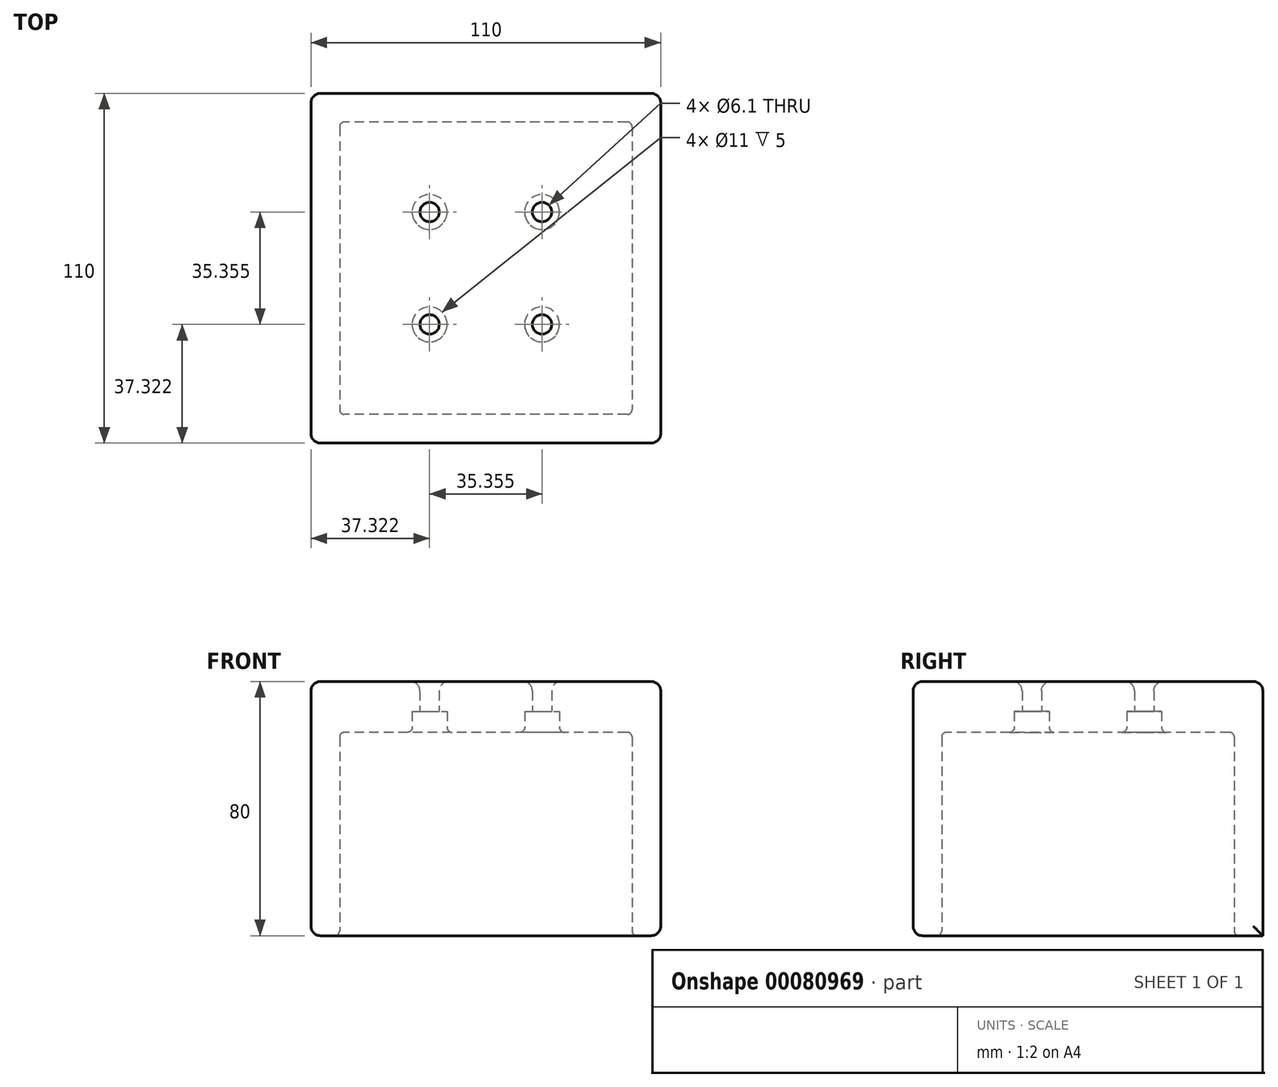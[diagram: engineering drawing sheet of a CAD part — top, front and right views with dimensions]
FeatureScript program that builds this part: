
annotation { "Feature Type Name" : "Feature", "Feature Type Description" : "" }
export const myFeature = defineFeature(function(context is Context, id is Id, definition is map)
    precondition{}
    {
        {
            var Q0;
            Q0=qCreatedBy(makeId("Top.planeOp"),FACE);
            var sketch = newSketch(context, id + "F0", { "sketchPlane" : qUnion([Q0])});
            skLineSegment(sketch, "E0.bottom", {"start": v(55, 55) * mm, "end": v(-55, 55) * mm});
            skLineSegment(sketch, "E0.top", {"start": v(55, -55) * mm, "end": v(-55, -55) * mm});
            skLineSegment(sketch, "E0.left", {"start": v(55, 55) * mm, "end": v(55, -55) * mm});
            skLineSegment(sketch, "E0.right", {"start": v(-55, 55) * mm, "end": v(-55, -55) * mm});
            skPoint(sketch, "E0.middle", {"position": v(0, 0) * mm});
            skLineSegment(sketch, "E1.bottom", {"start": v(46, 46) * mm, "end": v(-46, 46) * mm});
            skLineSegment(sketch, "E1.top", {"start": v(46, -46) * mm, "end": v(-46, -46) * mm});
            skLineSegment(sketch, "E1.left", {"start": v(46, 46) * mm, "end": v(46, -46) * mm});
            skLineSegment(sketch, "E1.right", {"start": v(-46, 46) * mm, "end": v(-46, -46) * mm});
            skSolve(sketch);
        }
        {
            var Q0;
            Q0=makeQuery(id+"F0.imprint","IMPRINT",FACE,{"disambiguationData":[TD([[makeQuery(id+"F0.imprint","IMPRINT",EDGE,{"derivedFrom":sQuery(id+"F0.wireOp",EDGE,"E0.bottom")}),1.0]])]});
            var Q1;
            Q1=makeQuery(id+"F0.imprint","IMPRINT",FACE,{"disambiguationData":[TD([[makeQuery(id+"F0.imprint","IMPRINT",EDGE,{"derivedFrom":sQuery(id+"F0.wireOp",EDGE,"E1.bottom")}),1.0]])]});
            extrude(context, id + "F1", {"entities" : qUnion([Q0, Q1]), "depth" : 80 * mm});
        }
        {
            var Q0;
            Q0=makeQuery(id+"F0.imprint","IMPRINT",FACE,{"disambiguationData":[TD([[makeQuery(id+"F0.imprint","IMPRINT",EDGE,{"derivedFrom":sQuery(id+"F0.wireOp",EDGE,"E1.bottom")}),1.0]])]});
            extrude(context, id + "F2", {"entities" : qUnion([Q0]), "operationType" : NewBodyOperationType.REMOVE, "depth" : 64 * mm});
        }
        {
            var Q0;
            Q0=makeQuery(id+"F2.boolean.opBoolean","COPY",FACE,{"derivedFrom":makeQuery(id+"F2.opExtrude","CAP_FACE",FACE,{"disambiguationData":[OSD([sQuery(id+"F0.wireOp",EDGE,"E1.bottom"),sQuery(id+"F0.wireOp",EDGE,"E1.top"),sQuery(id+"F0.wireOp",EDGE,"E1.left"),sQuery(id+"F0.wireOp",EDGE,"E1.right")])],"isStart":false})});
            var sketch = newSketch(context, id + "F3", { "sketchPlane" : qUnion([Q0])});
            skLineSegment(sketch, "E2", {"start": v(0, 0) * mm, "end": v(46, -46) * mm});
            skPoint(sketch, "E3", {"position": v(17.68, -17.68) * mm});
            skPoint(sketch, "E4.1.0", {"position": v(17.68, 17.68) * mm});
            skPoint(sketch, "E4.2.0", {"position": v(-17.68, 17.68) * mm});
            skPoint(sketch, "E4.3.0", {"position": v(-17.68, -17.68) * mm});
            skPoint(sketch, "E4.center", {"position": v(0, 0) * mm});
            skSolve(sketch);
        }
        {
            var Q0;
            Q0=sQuery(id+"F3.wireOp",VERTEX,"E4.1.0");
            var Q1;
            Q1=sQuery(id+"F3.wireOp",VERTEX,"E3");
            var Q2;
            Q2=sQuery(id+"F3.wireOp",VERTEX,"E4.3.0");
            var Q3;
            Q3=sQuery(id+"F3.wireOp",VERTEX,"E4.2.0");
            var Q4;
            Q4=makeQuery(id+"F1.opExtrude","SWEPT_BODY",BODY,{"disambiguationData":[OSD([sQuery(id+"F0.wireOp",EDGE,"E0.bottom"),sQuery(id+"F0.wireOp",EDGE,"E0.top"),sQuery(id+"F0.wireOp",EDGE,"E0.left"),sQuery(id+"F0.wireOp",EDGE,"E0.right")])]});
            hole(context, id + "F4", {"style" : HoleStyle.C_BORE, "endStyle" : HoleEndStyle.THROUGH, "holeDiameter" : 6.1 * mm, "cBoreDiameter" : 11 * mm, "cBoreDepth" : 6.5 * mm, "locations" : qUnion([Q0, Q1, Q2, Q3]), "scope" : qUnion([Q4]), "isTappedThrough" : true});
        }
        {
            var Q0;
            Q0=makeQuery(id+"F1.opExtrude","CAP_FACE",FACE,{"disambiguationData":[OSD([sQuery(id+"F0.wireOp",EDGE,"E0.bottom"),sQuery(id+"F0.wireOp",EDGE,"E0.top"),sQuery(id+"F0.wireOp",EDGE,"E0.left"),sQuery(id+"F0.wireOp",EDGE,"E0.right")])],"isStart":false});
            var Q1;
            Q1=makeQuery(id+"F1.opExtrude","SWEPT_FACE",FACE,{"disambiguationData":[OSD([sQuery(id+"F0.wireOp",EDGE,"E0.left")])]});
            var Q2;
            Q2=makeQuery(id+"F1.opExtrude","CAP_EDGE",EDGE,{"disambiguationData":[OSD([sQuery(id+"F0.wireOp",EDGE,"E0.right")])],"isStart":true});
            var Q3;
            Q3=makeQuery(id+"F1.opExtrude","SWEPT_FACE",FACE,{"disambiguationData":[OSD([sQuery(id+"F0.wireOp",EDGE,"E0.right")])]});
            var Q4;
            Q4=makeQuery(id+"F1.opExtrude","SWEPT_FACE",FACE,{"disambiguationData":[OSD([sQuery(id+"F0.wireOp",EDGE,"E0.top")])]});
            fillet(context, id + "F5", {"entities" : qUnion([Q0, Q1, Q2, Q3, Q4]), "radius" : 3 * mm, "tangentPropagation" : true, "allowEdgeOverflow" : false});
        }
        {
            var Q0;
            Q0=makeQuery(id+"F2.boolean.opBoolean","COPY",FACE,{"derivedFrom":makeQuery(id+"F2.opExtrude","CAP_FACE",FACE,{"disambiguationData":[OSD([sQuery(id+"F0.wireOp",EDGE,"E1.bottom"),sQuery(id+"F0.wireOp",EDGE,"E1.top"),sQuery(id+"F0.wireOp",EDGE,"E1.left"),sQuery(id+"F0.wireOp",EDGE,"E1.right")])],"isStart":false})});
            var Q1;
            Q1=makeQuery(id+"F2.boolean.opBoolean","COPY",FACE,{"derivedFrom":makeQuery(id+"F2.opExtrude","SWEPT_FACE",FACE,{"disambiguationData":[OSD([sQuery(id+"F0.wireOp",EDGE,"E1.top")])]})});
            var Q2;
            Q2=makeQuery(id+"F2.boolean.opBoolean","COPY",FACE,{"derivedFrom":makeQuery(id+"F2.opExtrude","SWEPT_FACE",FACE,{"disambiguationData":[OSD([sQuery(id+"F0.wireOp",EDGE,"E1.left")])]})});
            var Q3;
            Q3=makeQuery(id+"F2.boolean.opBoolean","COPY",FACE,{"derivedFrom":makeQuery(id+"F2.opExtrude","SWEPT_FACE",FACE,{"disambiguationData":[OSD([sQuery(id+"F0.wireOp",EDGE,"E1.right")])]})});
            var Q4;
            Q4=makeQuery(id+"F2.boolean.opBoolean","COPY",FACE,{"derivedFrom":makeQuery(id+"F2.opExtrude","SWEPT_FACE",FACE,{"disambiguationData":[OSD([sQuery(id+"F0.wireOp",EDGE,"E1.bottom")])]})});
            fillet(context, id + "F6", {"entities" : qUnion([Q0, Q1, Q2, Q3, Q4]), "radius" : 1.5 * mm, "tangentPropagation" : true, "allowEdgeOverflow" : false});
        }
    });
